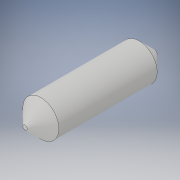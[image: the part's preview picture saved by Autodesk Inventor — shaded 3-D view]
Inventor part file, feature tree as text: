
AUTODESK INVENTOR PART (.ipt)
format: ipt  version: 2018 (Build 220112000, 112)  size: 97,280 bytes
history: native  units: in
note: dims shown in document units (in); Inventor stores cm internally (conversion verified against a paired STEP export)
features: extrude x1, chamfer x1, sketch x1
ambient origin geometry x8: Origin, YZ Plane, XZ Plane, XY Plane, X Axis, Y Axis, Z Axis, Center Point
bodies: Solid1 (feature_tree)
feature tree (3):
  extrude  "Extrusion1"  Depth=0.328in TaperAngle=0.0deg
  chamfer  "Chamfer1"  Distance=0.04in Angle=45.0deg
  sketch  "Sketch1"  dims[d0=0.091in d1=0.328in d2=0.0in d3=0.04in d4=0.125in d5=45.0deg]
